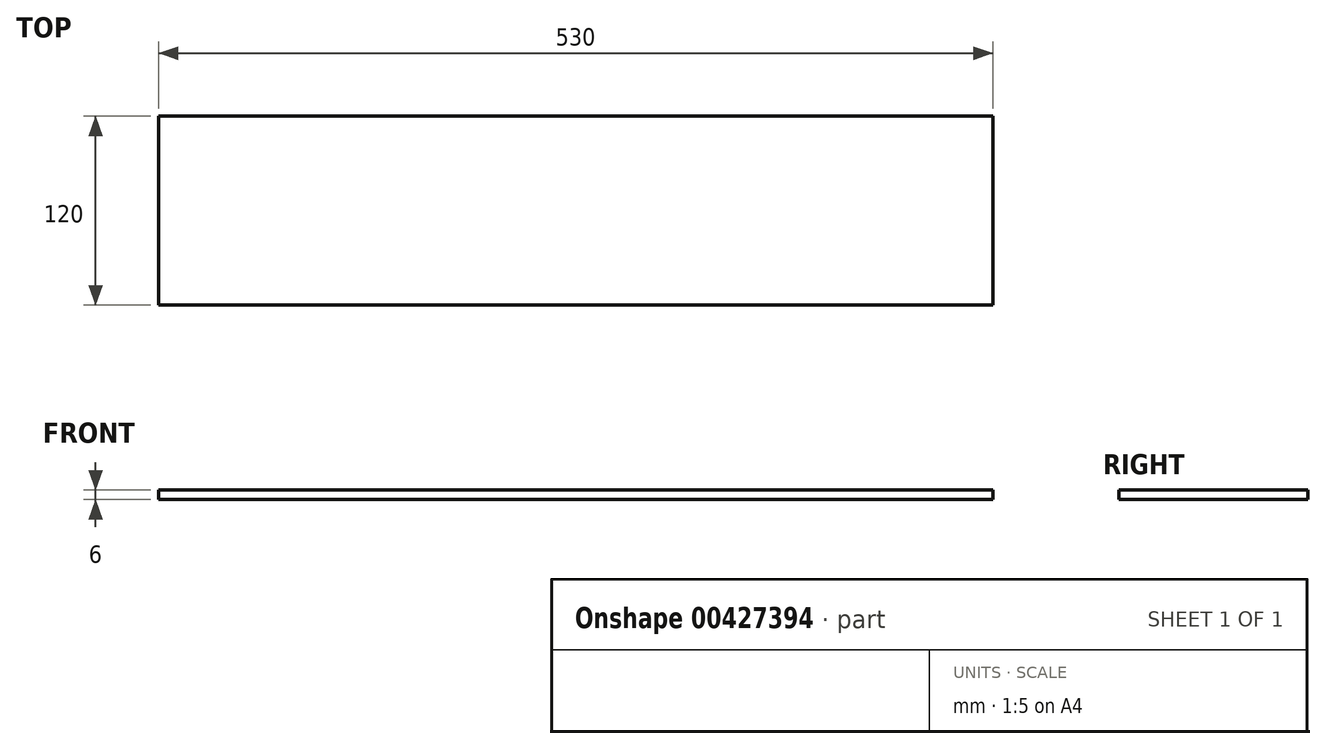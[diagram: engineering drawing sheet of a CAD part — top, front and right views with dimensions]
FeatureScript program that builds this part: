
annotation { "Feature Type Name" : "Feature", "Feature Type Description" : "" }
export const myFeature = defineFeature(function(context is Context, id is Id, definition is map)
    precondition{}
    {
        {
            var Q0;
            Q0=qCreatedBy(makeId("Top.planeOp"),FACE);
            var sketch = newSketch(context, id + "F0", { "sketchPlane" : qUnion([Q0])});
            skLineSegment(sketch, "E0.bottom", {"start": v(265, 60) * mm, "end": v(-265, 60) * mm});
            skLineSegment(sketch, "E0.top", {"start": v(265, -60) * mm, "end": v(-265, -60) * mm});
            skLineSegment(sketch, "E0.left", {"start": v(265, 60) * mm, "end": v(265, -60) * mm});
            skLineSegment(sketch, "E0.right", {"start": v(-265, 60) * mm, "end": v(-265, -60) * mm});
            skPoint(sketch, "E0.middle", {"position": v(0, 0) * mm});
            skSolve(sketch);
        }
        {
            var Q0;
            Q0=makeQuery(id+"F0.imprint","IMPRINT",FACE,{"disambiguationData":[TD([[makeQuery(id+"F0.imprint","IMPRINT",EDGE,{"derivedFrom":sQuery(id+"F0.wireOp",EDGE,"E0.bottom")}),1.0]])]});
            extrude(context, id + "F1", {"entities" : qUnion([Q0]), "depth" : 6 * mm});
        }
    });
